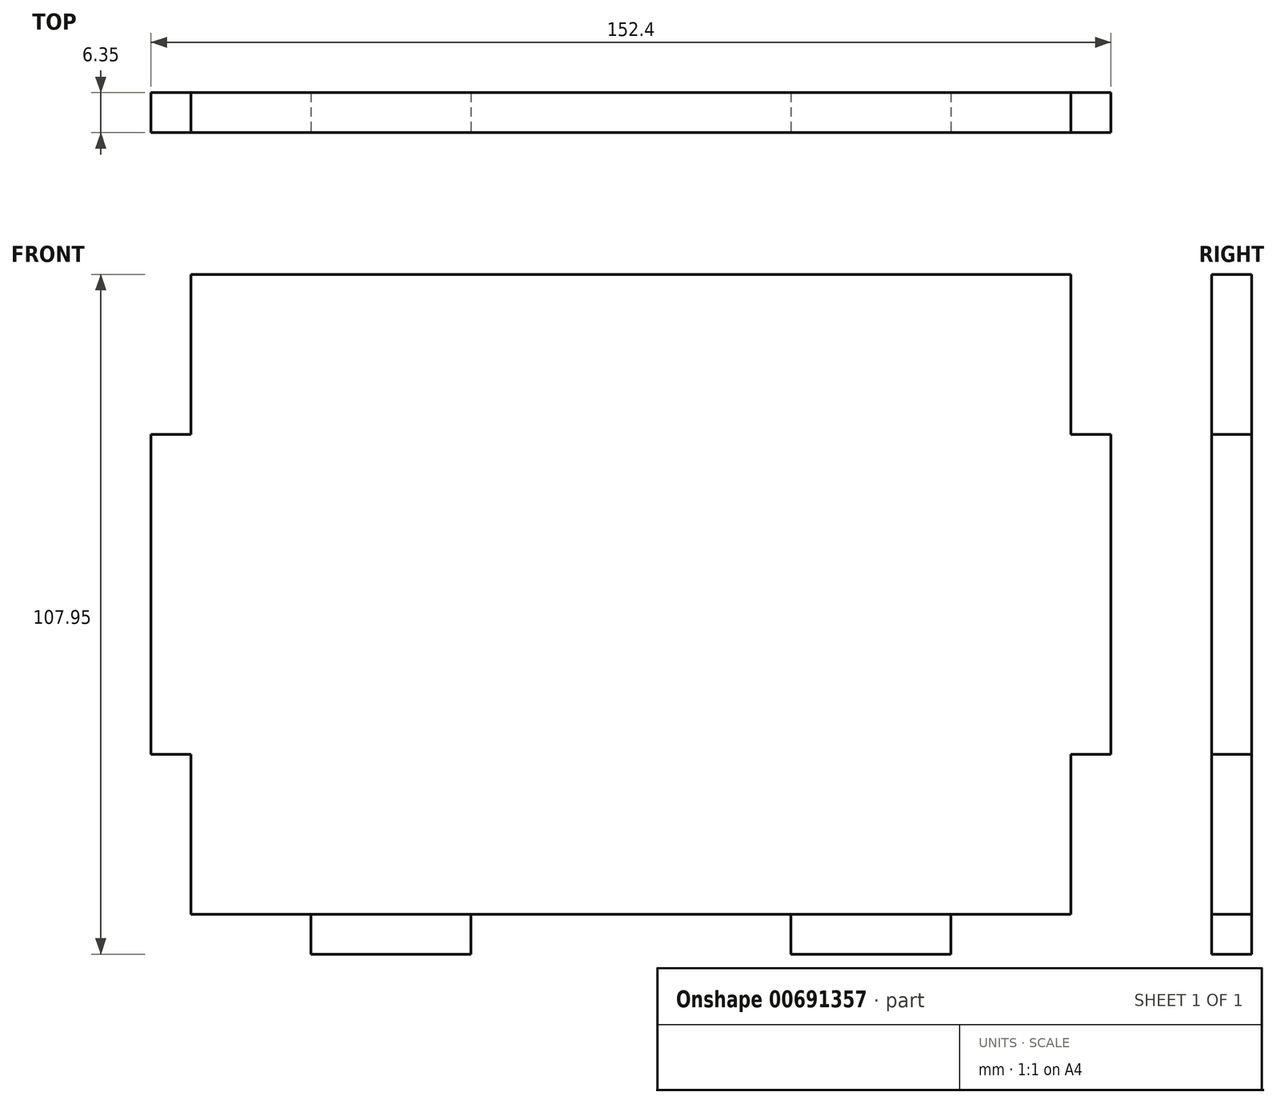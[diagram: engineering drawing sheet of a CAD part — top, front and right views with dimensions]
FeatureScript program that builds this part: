
annotation { "Feature Type Name" : "Feature", "Feature Type Description" : "" }
export const myFeature = defineFeature(function(context is Context, id is Id, definition is map)
    precondition{}
    {
        {
            var Q0;
            Q0=qCreatedBy(makeId("Front.planeOp"),FACE);
            var sketch = newSketch(context, id + "F0", { "sketchPlane" : qUnion([Q0])});
            skLineSegment(sketch, "E0.bottom", {"start": v(-76.2, 101.6) * mm, "end": v(76.2, 101.6) * mm});
            skLineSegment(sketch, "E0.top", {"start": v(-76.2, 0) * mm, "end": v(76.2, 0) * mm});
            skLineSegment(sketch, "E0.left", {"start": v(-76.2, 101.6) * mm, "end": v(-76.2, 0) * mm});
            skLineSegment(sketch, "E0.right", {"start": v(76.2, 101.6) * mm, "end": v(76.2, 0) * mm});
            skSolve(sketch);
        }
        {
            var Q0;
            Q0=qSketchRegion(id+"F0",true);
            extrude(context, id + "F1", {"entities" : qUnion([Q0]), "depth" : 6.35 * mm, "offsetDistance" : 25.4 * mm});
        }
        {
            var Q0;
            Q0=makeQuery(id+"F1.opExtrude","CAP_FACE",FACE,{"disambiguationData":[OSD([sQuery(id+"F0.wireOp",EDGE,"E0.bottom"),sQuery(id+"F0.wireOp",EDGE,"E0.top"),sQuery(id+"F0.wireOp",EDGE,"E0.left"),sQuery(id+"F0.wireOp",EDGE,"E0.right")])],"isStart":false});
            var sketch = newSketch(context, id + "F2", { "sketchPlane" : qUnion([Q0])});
            skLineSegment(sketch, "E1.bottom", {"start": v(50.8, 0) * mm, "end": v(25.4, 0) * mm});
            skLineSegment(sketch, "E1.top", {"start": v(50.8, -6.35) * mm, "end": v(25.4, -6.35) * mm});
            skLineSegment(sketch, "E1.left", {"start": v(50.8, -6.35) * mm, "end": v(50.8, 0) * mm});
            skLineSegment(sketch, "E1.right", {"start": v(25.4, -6.35) * mm, "end": v(25.4, 0) * mm});
            skLineSegment(sketch, "E2.MirrorCS", {"start": v(-50.8, 0) * mm, "end": v(-25.4, 0) * mm});
            skLineSegment(sketch, "E3.MirrorCS", {"start": v(-50.8, -6.35) * mm, "end": v(-25.4, -6.35) * mm});
            skLineSegment(sketch, "E4.MirrorCS", {"start": v(-50.8, -6.35) * mm, "end": v(-50.8, 0) * mm});
            skLineSegment(sketch, "E5.MirrorCS", {"start": v(-25.4, -6.35) * mm, "end": v(-25.4, 0) * mm});
            skSolve(sketch);
        }
        {
            var Q0;
            Q0=qSketchRegion(id+"F2",true);
            extrude(context, id + "F3", {"entities" : qUnion([Q0]), "oppositeDirection" : true, "depth" : 6.35 * mm, "offsetDistance" : 25.4 * mm});
        }
        {
            var Q0;
            Q0=makeQuery(id+"F1.opExtrude","CAP_FACE",FACE,{"disambiguationData":[OSD([sQuery(id+"F0.wireOp",EDGE,"E0.bottom"),sQuery(id+"F0.wireOp",EDGE,"E0.top"),sQuery(id+"F0.wireOp",EDGE,"E0.left"),sQuery(id+"F0.wireOp",EDGE,"E0.right")])],"isStart":false});
            var sketch = newSketch(context, id + "F4", { "sketchPlane" : qUnion([Q0])});
            skLineSegment(sketch, "E6.bottom", {"start": v(76.2, 101.6) * mm, "end": v(69.85, 101.6) * mm});
            skLineSegment(sketch, "E6.top", {"start": v(76.2, 76.2) * mm, "end": v(69.85, 76.2) * mm});
            skLineSegment(sketch, "E6.left", {"start": v(76.2, 101.6) * mm, "end": v(76.2, 76.2) * mm});
            skLineSegment(sketch, "E6.right", {"start": v(69.85, 101.6) * mm, "end": v(69.85, 76.2) * mm});
            skLineSegment(sketch, "E7.bottom", {"start": v(76.2, 0) * mm, "end": v(69.85, 0) * mm});
            skLineSegment(sketch, "E7.top", {"start": v(76.2, 25.4) * mm, "end": v(69.85, 25.4) * mm});
            skLineSegment(sketch, "E7.left", {"start": v(76.2, 0) * mm, "end": v(76.2, 25.4) * mm});
            skLineSegment(sketch, "E7.right", {"start": v(69.85, 0) * mm, "end": v(69.85, 25.4) * mm});
            skLineSegment(sketch, "E8.MirrorCS", {"start": v(-69.85, 0) * mm, "end": v(-69.85, 25.4) * mm});
            skLineSegment(sketch, "E9.MirrorCS", {"start": v(-76.2, 0) * mm, "end": v(-76.2, 25.4) * mm});
            skLineSegment(sketch, "E10.MirrorCS", {"start": v(-76.2, 25.4) * mm, "end": v(-69.85, 25.4) * mm});
            skLineSegment(sketch, "E11.MirrorCS", {"start": v(-76.2, 101.6) * mm, "end": v(-69.85, 101.6) * mm});
            skLineSegment(sketch, "E12.MirrorCS", {"start": v(-76.2, 76.2) * mm, "end": v(-69.85, 76.2) * mm});
            skLineSegment(sketch, "E13.MirrorCS", {"start": v(-76.2, 101.6) * mm, "end": v(-76.2, 76.2) * mm});
            skLineSegment(sketch, "E14.MirrorCS", {"start": v(-76.2, 0) * mm, "end": v(-69.85, 0) * mm});
            skLineSegment(sketch, "E15.MirrorCS", {"start": v(-69.85, 101.6) * mm, "end": v(-69.85, 76.2) * mm});
            skSolve(sketch);
        }
        {
            var Q0;
            Q0=qSketchRegion(id+"F4",true);
            extrude(context, id + "F5", {"entities" : qUnion([Q0]), "operationType" : NewBodyOperationType.REMOVE, "oppositeDirection" : true, "depth" : 25.4 * mm, "offsetDistance" : 25.4 * mm});
        }
    });
